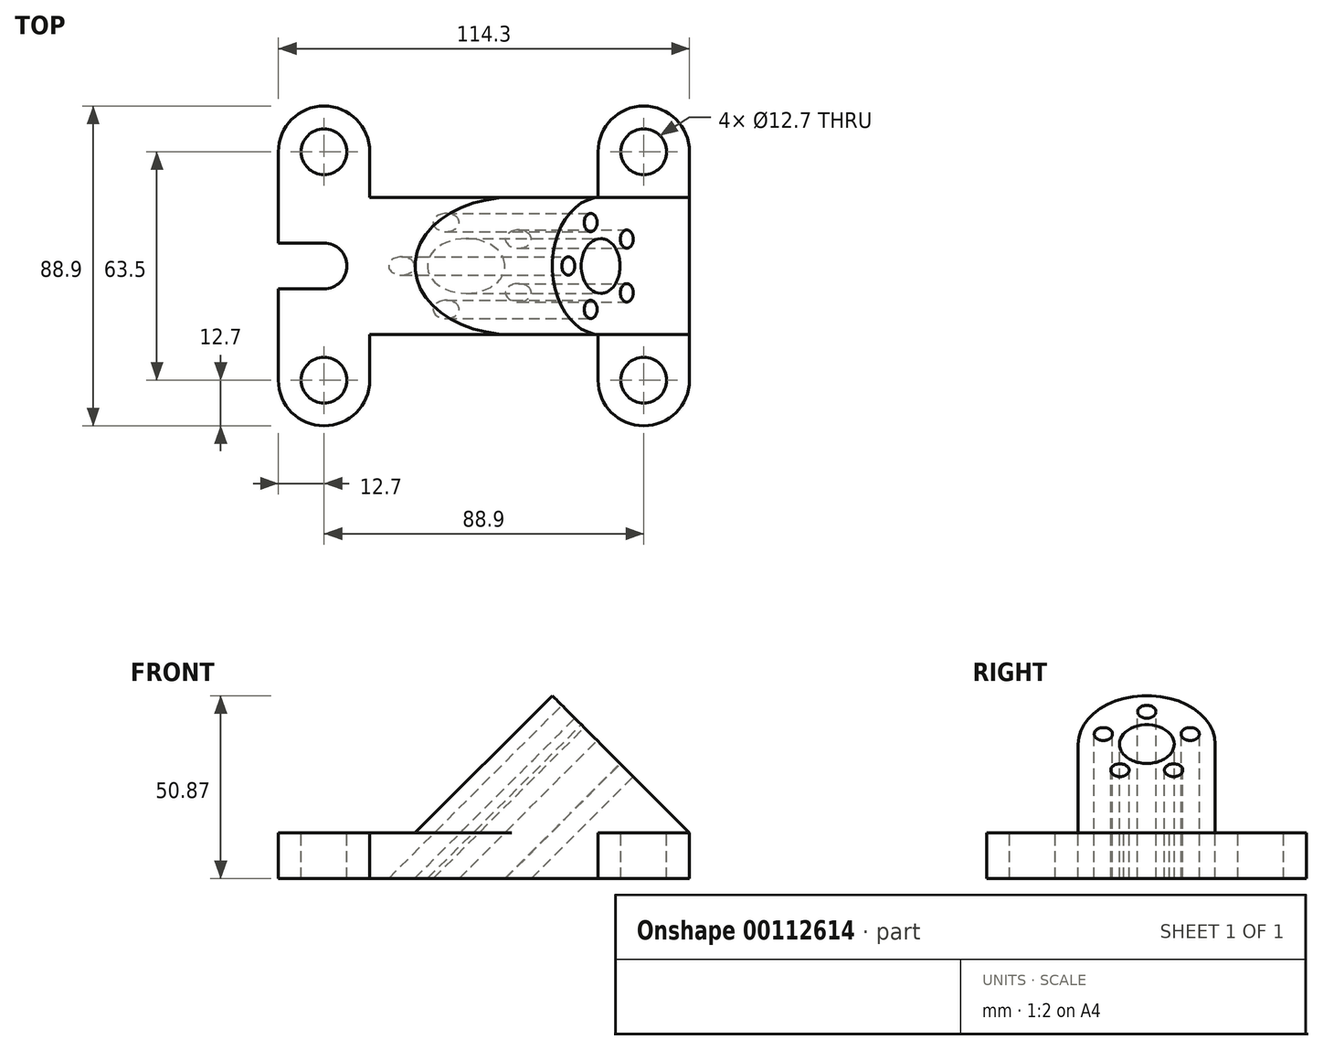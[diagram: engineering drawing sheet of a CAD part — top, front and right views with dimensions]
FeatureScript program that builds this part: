
annotation { "Feature Type Name" : "Feature", "Feature Type Description" : "" }
export const myFeature = defineFeature(function(context is Context, id is Id, definition is map)
    precondition{}
    {
        {
            var Q0;
            Q0=qCreatedBy(makeId("Top.planeOp"),FACE);
            var sketch = newSketch(context, id + "F0", { "sketchPlane" : qUnion([Q0])});
            skLineSegment(sketch, "E0", {"start": v(0, -19.05) * mm, "end": v(0, 19.05) * mm});
            skLineSegment(sketch, "E1", {"start": v(0, 19.05) * mm, "end": v(31.75, 19.05) * mm});
            skLineSegment(sketch, "E2", {"start": v(31.75, 19.05) * mm, "end": v(31.75, 31.75) * mm});
            skLineSegment(sketch, "E3", {"start": v(31.75, 31.75) * mm, "end": v(44.45, 31.75) * mm, "construction": true});
            skLineSegment(sketch, "E4", {"start": v(44.45, 31.75) * mm, "end": v(57.15, 31.75) * mm, "construction": true});
            skLineSegment(sketch, "E5", {"start": v(57.15, 31.75) * mm, "end": v(57.15, -31.75) * mm});
            skLineSegment(sketch, "E6", {"start": v(57.15, -31.75) * mm, "end": v(44.45, -31.75) * mm, "construction": true});
            skLineSegment(sketch, "E7", {"start": v(44.45, -31.75) * mm, "end": v(31.75, -31.75) * mm, "construction": true});
            skLineSegment(sketch, "E8", {"start": v(31.75, -31.75) * mm, "end": v(31.75, -19.05) * mm});
            skLineSegment(sketch, "E9", {"start": v(31.75, -19.05) * mm, "end": v(0, -19.05) * mm});
            skCircle(sketch, "E10", {"center": v(44.45, 31.75) * mm, "radius": 6.35 * mm});
            skCircle(sketch, "E11", {"center": v(44.45, -31.75) * mm, "radius": 6.35 * mm});
            skArc(sketch, "E12", {"start": v(31.75, 31.75) * mm, "mid": v(44.45, 44.45) * mm, "end": v(57.15, 31.75) * mm});
            skArc(sketch, "E13", {"start": v(31.75, -31.75) * mm, "mid": v(44.45, -44.45) * mm, "end": v(57.15, -31.75) * mm});
            skLineSegment(sketch, "E14", {"start": v(0, -29.52) * mm, "end": v(0, 37.3) * mm, "construction": true});
            skLineSegment(sketch, "E15.MirrorCS", {"start": v(-31.75, -19.05) * mm, "end": v(0, -19.05) * mm});
            skLineSegment(sketch, "E16.MirrorCS", {"start": v(-31.75, -31.75) * mm, "end": v(-31.75, -19.05) * mm});
            skArc(sketch, "E17.MirrorCS", {"start": v(-31.75, -31.75) * mm, "mid": v(-44.45, -44.45) * mm, "end": v(-57.15, -31.75) * mm});
            skCircle(sketch, "E18.MirrorC", {"center": v(-44.45, -31.75) * mm, "radius": 6.35 * mm});
            skCircle(sketch, "E19.MirrorC", {"center": v(-44.45, 31.75) * mm, "radius": 6.35 * mm});
            skArc(sketch, "E20.MirrorCS", {"start": v(-31.75, 31.75) * mm, "mid": v(-44.45, 44.45) * mm, "end": v(-57.15, 31.75) * mm});
            skLineSegment(sketch, "E21.MirrorCS", {"start": v(-31.75, 19.05) * mm, "end": v(-31.75, 31.75) * mm});
            skLineSegment(sketch, "E22.MirrorCS", {"start": v(0, 19.05) * mm, "end": v(-31.75, 19.05) * mm});
            skLineSegment(sketch, "E23", {"start": v(-57.15, 31.75) * mm, "end": v(-57.15, 6.35) * mm});
            skLineSegment(sketch, "E24", {"start": v(-57.15, 6.35) * mm, "end": v(-57.15, -6.35) * mm, "construction": true});
            skLineSegment(sketch, "E25", {"start": v(-57.15, -6.35) * mm, "end": v(-57.15, -31.75) * mm});
            skLineSegment(sketch, "E26", {"start": v(-57.15, -6.35) * mm, "end": v(-44.45, -6.35) * mm});
            skLineSegment(sketch, "E27", {"start": v(-44.45, -6.35) * mm, "end": v(-44.45, 6.35) * mm, "construction": true});
            skLineSegment(sketch, "E28", {"start": v(-44.45, 6.35) * mm, "end": v(-57.15, 6.35) * mm});
            skArc(sketch, "E29", {"start": v(-44.45, -6.35) * mm, "mid": v(-38.1, 0) * mm, "end": v(-44.45, 6.35) * mm});
            skSolve(sketch);
        }
        {
            var Q0;
            Q0 = qSketchRegion(id + "F0", true);
            extrude(context, id + "F1", {"entities" : qUnion([Q0]), "oppositeDirection" : true, "depth" : 12.7 * mm});
        }
        {
            var Q0;
            Q0=makeQuery(id+"F1.opExtrude","CAP_EDGE",EDGE,{"disambiguationData":[OSD([sQuery(id+"F0.wireOp",EDGE,"E5")])],"isStart":true});
            var Q1;
            Q1=makeQuery(id+"F1.opExtrude","CAP_FACE",FACE,{"disambiguationData":[OSD([sQuery(id+"F0.wireOp",EDGE,"E1"),sQuery(id+"F0.wireOp",EDGE,"E2"),sQuery(id+"F0.wireOp",EDGE,"E5"),sQuery(id+"F0.wireOp",EDGE,"E8"),sQuery(id+"F0.wireOp",EDGE,"E9"),sQuery(id+"F0.wireOp",EDGE,"E10"),sQuery(id+"F0.wireOp",EDGE,"E11"),sQuery(id+"F0.wireOp",EDGE,"E12"),sQuery(id+"F0.wireOp",EDGE,"E13"),sQuery(id+"F0.wireOp",EDGE,"E15.MirrorCS"),sQuery(id+"F0.wireOp",EDGE,"E16.MirrorCS"),sQuery(id+"F0.wireOp",EDGE,"E17.MirrorCS"),sQuery(id+"F0.wireOp",EDGE,"E18.MirrorC"),sQuery(id+"F0.wireOp",EDGE,"E19.MirrorC"),sQuery(id+"F0.wireOp",EDGE,"E20.MirrorCS"),sQuery(id+"F0.wireOp",EDGE,"E21.MirrorCS"),sQuery(id+"F0.wireOp",EDGE,"E22.MirrorCS"),sQuery(id+"F0.wireOp",EDGE,"E23"),sQuery(id+"F0.wireOp",EDGE,"E25"),sQuery(id+"F0.wireOp",EDGE,"E26"),sQuery(id+"F0.wireOp",EDGE,"E28"),sQuery(id+"F0.wireOp",EDGE,"E29")])],"isStart":true});
            cPlane(context, id + "F2", {"entities" : qUnion([Q0, Q1]), "cplaneType" : CPlaneType.LINE_ANGLE, "offset" : 25.4 * mm, "angle" : 135 * degree, "width" : 152.4 * mm, "height" : 152.4 * mm});
        }
        {
            var Q0;
            Q0=qCreatedBy(id+"F2.planeOp",FACE);
            var sketch = newSketch(context, id + "F3", { "sketchPlane" : qUnion([Q0])});
            skLineSegment(sketch, "E30", {"start": v(0, -40.41) * mm, "end": v(-19.05, -40.41) * mm});
            skLineSegment(sketch, "E31", {"start": v(-19.05, -40.41) * mm, "end": v(-19.05, -5.49) * mm});
            skLineSegment(sketch, "E32", {"start": v(-19.05, -5.49) * mm, "end": v(19.05, -5.49) * mm, "construction": true});
            skLineSegment(sketch, "E33", {"start": v(19.05, -5.49) * mm, "end": v(19.05, -40.41) * mm});
            skLineSegment(sketch, "E34", {"start": v(19.05, -40.41) * mm, "end": v(0, -40.41) * mm});
            skArc(sketch, "E35", {"start": v(19.05, -5.49) * mm, "mid": v(0, 13.56) * mm, "end": v(-19.05, -5.49) * mm});
            skCircle(sketch, "E36", {"center": v(0, -5.49) * mm, "radius": 7.62 * mm});
            skCircle(sketch, "E37", {"center": v(0, 7.21) * mm, "radius": 2.54 * mm});
            skCircle(sketch, "E38.1.0", {"center": v(12.08, -1.56) * mm, "radius": 2.54 * mm});
            skCircle(sketch, "E38.2.0", {"center": v(7.46, -15.76) * mm, "radius": 2.54 * mm});
            skLineSegment(sketch, "E38.anchor1", {"start": v(0, -5.49) * mm, "end": v(0, 7.21) * mm, "construction": true});
            skLineSegment(sketch, "E38.anchor2", {"start": v(0, -5.49) * mm, "end": v(7.46, -15.76) * mm, "construction": true});
            skCircle(sketch, "E39.1.0", {"center": v(-7.46, -15.76) * mm, "radius": 2.54 * mm});
            skCircle(sketch, "E39.2.0", {"center": v(-12.08, -1.56) * mm, "radius": 2.54 * mm});
            skLineSegment(sketch, "E39.anchor2", {"start": v(0, -5.49) * mm, "end": v(-12.08, -1.56) * mm, "construction": true});
            skSolve(sketch);
        }
        {
            var Q0;
            Q0 = qSketchRegion(id + "F3", true);
            extrude(context, id + "F4", {"entities" : qUnion([Q0]), "operationType" : NewBodyOperationType.ADD, "endBound" : BoundingType.UP_TO_NEXT, "oppositeDirection" : true, "depth" : 25.4 * mm});
        }
        {
            var Q0;
            Q0=makeQuery(id+"F3.imprint","IMPRINT",FACE,{"disambiguationData":[TD([[makeQuery(id+"F3.imprint","IMPRINT",EDGE,{"derivedFrom":sQuery(id+"F3.wireOp",EDGE,"E37")}),1.0]])]});
            var Q1;
            Q1=makeQuery(id+"F3.imprint","IMPRINT",FACE,{"disambiguationData":[TD([[makeQuery(id+"F3.imprint","IMPRINT",EDGE,{"derivedFrom":sQuery(id+"F3.wireOp",EDGE,"E38.1.0")}),1.0]])]});
            var Q2;
            Q2=makeQuery(id+"F3.imprint","IMPRINT",FACE,{"disambiguationData":[TD([[makeQuery(id+"F3.imprint","IMPRINT",EDGE,{"derivedFrom":sQuery(id+"F3.wireOp",EDGE,"E38.2.0")}),1.0]])]});
            var Q3;
            Q3=makeQuery(id+"F3.imprint","IMPRINT",FACE,{"disambiguationData":[TD([[makeQuery(id+"F3.imprint","IMPRINT",EDGE,{"derivedFrom":sQuery(id+"F3.wireOp",EDGE,"E39.1.0")}),1.0]])]});
            var Q4;
            Q4=makeQuery(id+"F3.imprint","IMPRINT",FACE,{"disambiguationData":[TD([[makeQuery(id+"F3.imprint","IMPRINT",EDGE,{"derivedFrom":sQuery(id+"F3.wireOp",EDGE,"E39.2.0")}),1.0]])]});
            var Q5;
            Q5=makeQuery(id+"F3.imprint","IMPRINT",FACE,{"disambiguationData":[TD([[makeQuery(id+"F3.imprint","IMPRINT",EDGE,{"derivedFrom":sQuery(id+"F3.wireOp",EDGE,"E36")}),1.0]])]});
            extrude(context, id + "F5", {"entities" : qUnion([Q0, Q1, Q2, Q3, Q4, Q5]), "operationType" : NewBodyOperationType.REMOVE, "endBound" : BoundingType.THROUGH_ALL, "oppositeDirection" : true, "depth" : 25.4 * mm});
        }
    });
